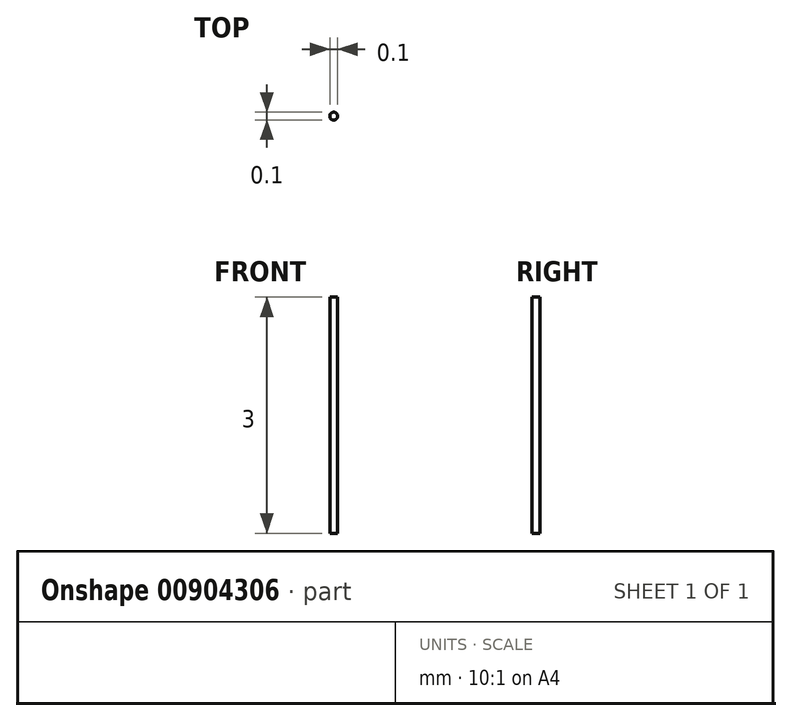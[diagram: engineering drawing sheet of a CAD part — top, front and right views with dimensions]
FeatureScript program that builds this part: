
annotation { "Feature Type Name" : "Feature", "Feature Type Description" : "" }
export const myFeature = defineFeature(function(context is Context, id is Id, definition is map)
    precondition{}
    {
        {
            var Q0;
            Q0=qCreatedBy(makeId("Front.planeOp"),FACE);
            var sketch = newSketch(context, id + "F0", { "sketchPlane" : qUnion([Q0])});
            skLineSegment(sketch, "E0.bottom", {"start": v(0, 0) * mm, "end": v(-0.05, 0) * mm});
            skLineSegment(sketch, "E0.top", {"start": v(0, 3) * mm, "end": v(-0.05, 3) * mm});
            skLineSegment(sketch, "E0.left", {"start": v(0, 0) * mm, "end": v(0, 3) * mm});
            skLineSegment(sketch, "E0.right", {"start": v(-0.05, 0) * mm, "end": v(-0.05, 3) * mm});
            skSolve(sketch);
        }
        {
            var Q0;
            Q0=makeQuery(id+"F0.imprint","IMPRINT",FACE,{"disambiguationData":[TD([[makeQuery(id+"F0.imprint","IMPRINT",EDGE,{"derivedFrom":sQuery(id+"F0.wireOp",EDGE,"E0.bottom")}),-1.0]])]});
            var Q1;
            Q1=sQuery(id+"F0.wireOp",EDGE,"E0.left");
            revolve(context, id + "F1", {"surfaceOperationType" : NewSurfaceOperationType.NEW, "entities" : qUnion([Q0]), "axis" : qUnion([Q1]), "revolveType" : RevolveType.FULL});
        }
    });
